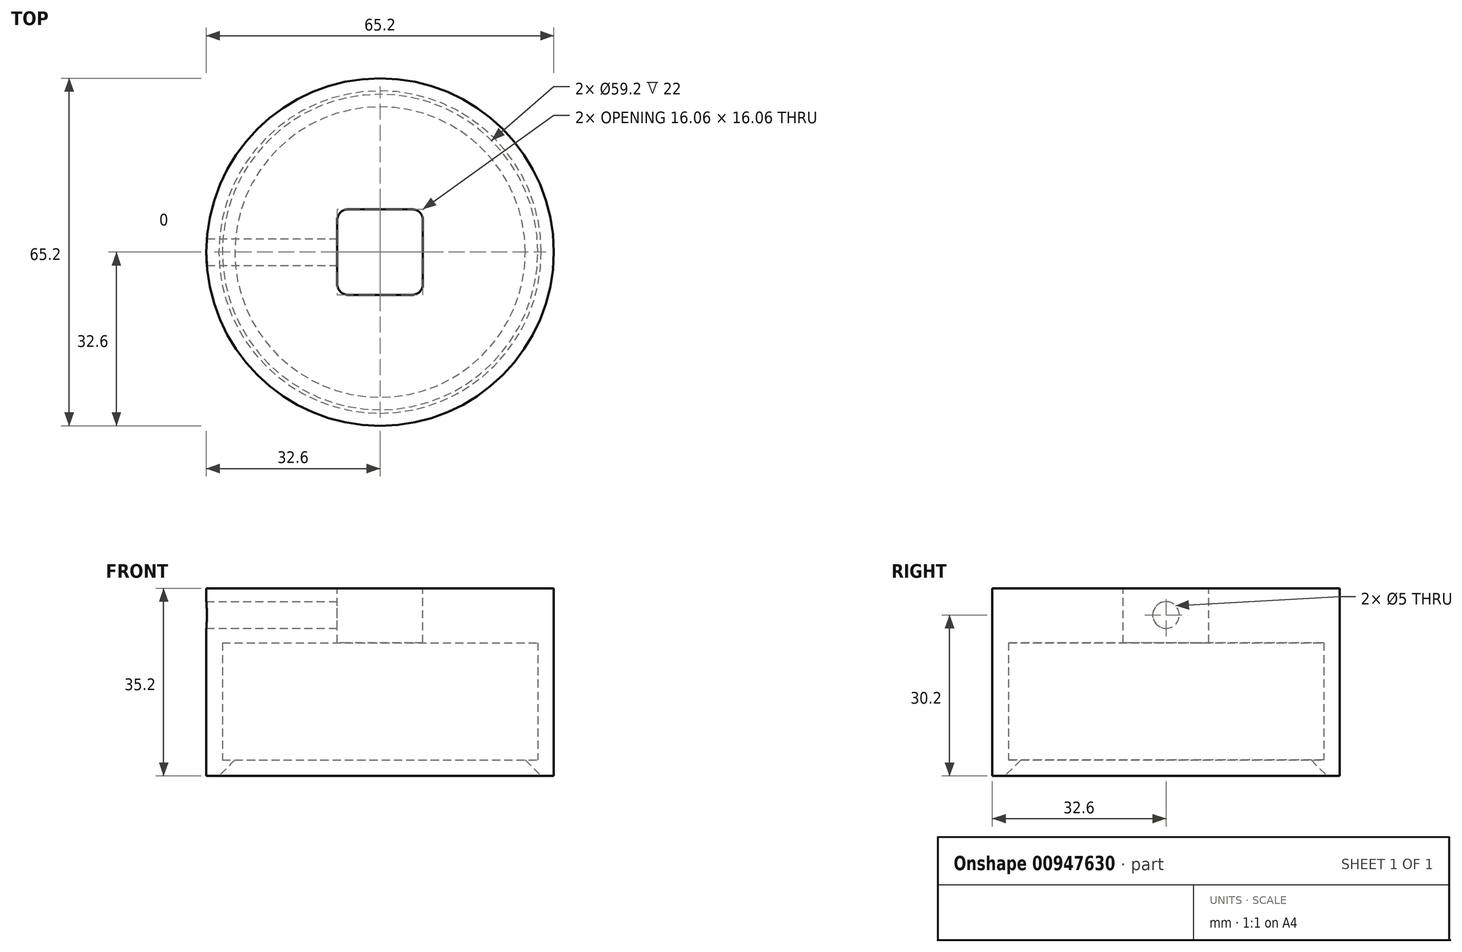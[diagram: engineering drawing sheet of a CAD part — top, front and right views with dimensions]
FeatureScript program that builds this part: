
annotation { "Feature Type Name" : "Feature", "Feature Type Description" : "" }
export const myFeature = defineFeature(function(context is Context, id is Id, definition is map)
    precondition{}
    {
        {
            var Q0;
            Q0=qCreatedBy(makeId("Front.planeOp"),FACE);
            var sketch = newSketch(context, id + "F0", { "sketchPlane" : qUnion([Q0])});
            skLineSegment(sketch, "E0", {"start": v(0, 0) * mm, "end": v(-32.6, 0) * mm});
            skLineSegment(sketch, "E1", {"start": v(-32.6, 0) * mm, "end": v(-32.6, -35.2) * mm});
            skLineSegment(sketch, "E2", {"start": v(-32.6, -35.2) * mm, "end": v(-30.25, -35.2) * mm});
            skLineSegment(sketch, "E3", {"start": v(-30.25, -35.2) * mm, "end": v(-27.25, -32.2) * mm});
            skLineSegment(sketch, "E4", {"start": v(-27.25, -32.2) * mm, "end": v(-29.6, -32.2) * mm});
            skLineSegment(sketch, "E5", {"start": v(-29.6, -32.2) * mm, "end": v(-29.6, -10.2) * mm});
            skLineSegment(sketch, "E6", {"start": v(-29.6, -10.2) * mm, "end": v(0, -10.2) * mm});
            skLineSegment(sketch, "E7", {"start": v(0, -10.2) * mm, "end": v(0, 0) * mm});
            skSolve(sketch);
        }
        {
            var Q0;
            Q0=makeQuery(id+"F0.imprint","IMPRINT",FACE,{"disambiguationData":[TD([[makeQuery(id+"F0.imprint","IMPRINT",EDGE,{"derivedFrom":sQuery(id+"F0.wireOp",EDGE,"E0")}),1.0]])]});
            var Q1;
            Q1=sQuery(id+"F0.wireOp",EDGE,"E7");
            revolve(context, id + "F1", {"surfaceOperationType" : NewSurfaceOperationType.NEW, "entities" : qUnion([Q0]), "axis" : qUnion([Q1]), "revolveType" : RevolveType.FULL});
        }
        {
            var Q0;
            Q0=makeQuery(id+"F1.opRevolve","SWEPT_FACE",FACE,{"disambiguationData":[OSD([sQuery(id+"F0.wireOp",EDGE,"E0")])]});
            var sketch = newSketch(context, id + "F2", { "sketchPlane" : qUnion([Q0])});
            skLineSegment(sketch, "E8.bottom", {"start": v(6.03, 8.03) * mm, "end": v(-6.03, 8.03) * mm});
            skLineSegment(sketch, "E8.top", {"start": v(6.03, -8.03) * mm, "end": v(-6.03, -8.03) * mm});
            skLineSegment(sketch, "E8.left", {"start": v(8.03, 6.03) * mm, "end": v(8.03, -6.03) * mm});
            skLineSegment(sketch, "E8.right", {"start": v(-8.03, 6.03) * mm, "end": v(-8.03, -6.03) * mm});
            skPoint(sketch, "E8.middle", {"position": v(0, 0) * mm});
            skPoint(sketch, "E9.visualSharp", {"position": v(-8.03, 8.03) * mm});
            skArc(sketch, "E9.filletArc", {"start": v(-6.03, 8.03) * mm, "mid": v(-7.44, 7.44) * mm, "end": v(-8.03, 6.03) * mm});
            skPoint(sketch, "E10.visualSharp", {"position": v(8.03, 8.03) * mm});
            skArc(sketch, "E10.filletArc", {"start": v(8.03, 6.03) * mm, "mid": v(7.44, 7.44) * mm, "end": v(6.03, 8.03) * mm});
            skPoint(sketch, "E11.visualSharp", {"position": v(8.03, -8.03) * mm});
            skArc(sketch, "E11.filletArc", {"start": v(6.03, -8.03) * mm, "mid": v(7.44, -7.44) * mm, "end": v(8.03, -6.03) * mm});
            skPoint(sketch, "E12.visualSharp", {"position": v(-8.03, -8.03) * mm});
            skArc(sketch, "E12.filletArc", {"start": v(-8.03, -6.03) * mm, "mid": v(-7.44, -7.44) * mm, "end": v(-6.03, -8.03) * mm});
            skSolve(sketch);
        }
        {
            var Q0;
            Q0 = qSketchRegion(id + "F2", true);
            extrude(context, id + "F3", {"entities" : qUnion([Q0]), "operationType" : NewBodyOperationType.REMOVE, "oppositeDirection" : true, "depth" : 25 * mm, "offsetDistance" : 25 * mm});
        }
        {
            var Q0;
            Q0=makeQuery(id+"F3.boolean.opBoolean","COPY",FACE,{"derivedFrom":makeQuery(id+"F3.opExtrude","SWEPT_FACE",FACE,{"disambiguationData":[OSD([sQuery(id+"F2.wireOp",EDGE,"E8.right")])]})});
            var sketch = newSketch(context, id + "F4", { "sketchPlane" : qUnion([Q0])});
            skCircle(sketch, "E13", {"center": v(0, -5) * mm, "radius": 2.5 * mm});
            skSolve(sketch);
        }
        {
            var Q0;
            Q0 = qSketchRegion(id + "F4", true);
            extrude(context, id + "F5", {"entities" : qUnion([Q0]), "operationType" : NewBodyOperationType.REMOVE, "endBound" : BoundingType.THROUGH_ALL, "oppositeDirection" : true, "depth" : 25 * mm, "offsetDistance" : 25 * mm});
        }
    });
